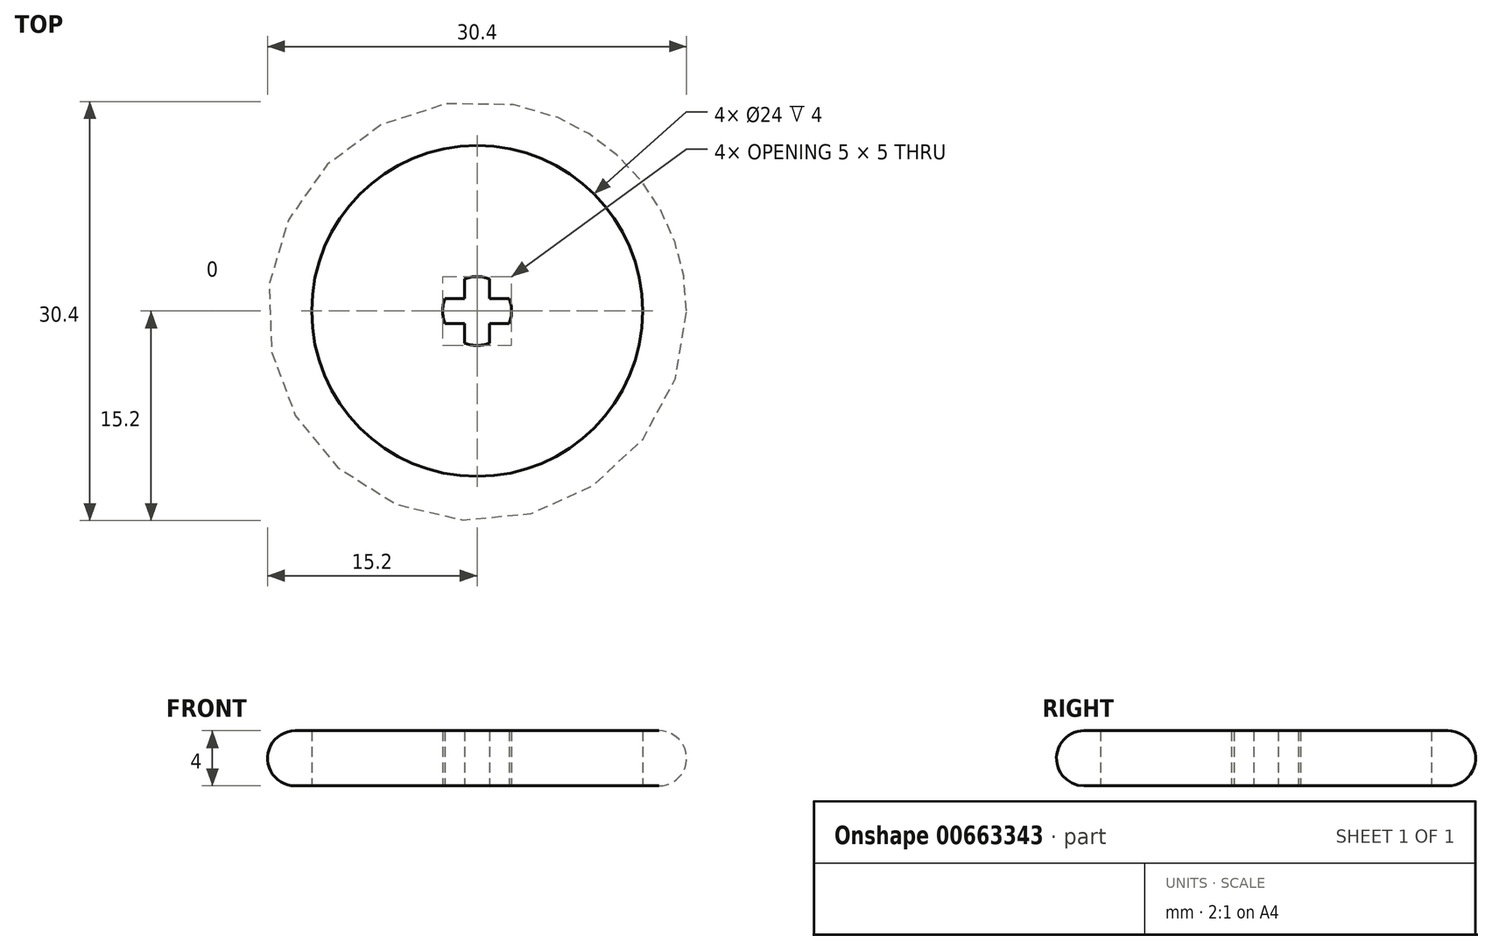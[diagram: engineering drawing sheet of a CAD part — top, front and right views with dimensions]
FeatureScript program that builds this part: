
annotation { "Feature Type Name" : "Feature", "Feature Type Description" : "" }
export const myFeature = defineFeature(function(context is Context, id is Id, definition is map)
    precondition{}
    {
        {
            var Q0;
            Q0=qCreatedBy(makeId("Top.planeOp"),FACE);
            var sketch = newSketch(context, id + "F0", { "sketchPlane" : qUnion([Q0])});
            skCircle(sketch, "E0", {"center": v(0, 0) * mm, "radius": 12 * mm});
            skArc(sketch, "E1", {"start": v(-0.9, -2.33) * mm, "mid": v(0, -2.5) * mm, "end": v(0.9, -2.33) * mm});
            skLineSegment(sketch, "E2.left", {"start": v(0.9, 2.33) * mm, "end": v(0.9, 0.9) * mm});
            skLineSegment(sketch, "E2.right", {"start": v(-0.9, 2.33) * mm, "end": v(-0.9, 0.9) * mm});
            skLineSegment(sketch, "E3.bottom", {"start": v(2.33, 0.9) * mm, "end": v(0.9, 0.9) * mm});
            skLineSegment(sketch, "E3.top", {"start": v(2.33, -0.9) * mm, "end": v(0.9, -0.9) * mm});
            skLineSegment(sketch, "E4.trimOffspring", {"start": v(-0.9, -0.9) * mm, "end": v(-0.9, -2.33) * mm});
            skLineSegment(sketch, "E5.trimOffspring", {"start": v(-0.9, 0.9) * mm, "end": v(-2.33, 0.9) * mm});
            skLineSegment(sketch, "E6.trimOffspring", {"start": v(0.9, -0.9) * mm, "end": v(0.9, -2.33) * mm});
            skLineSegment(sketch, "E7.trimOffspring", {"start": v(-0.9, -0.9) * mm, "end": v(-2.33, -0.9) * mm});
            skArc(sketch, "E8.trimOffspring", {"start": v(-2.33, 0.9) * mm, "mid": v(-2.5, 0) * mm, "end": v(-2.33, -0.9) * mm});
            skArc(sketch, "E9.trimOffspring", {"start": v(0.9, 2.33) * mm, "mid": v(0, 2.5) * mm, "end": v(-0.9, 2.33) * mm});
            skArc(sketch, "E10.trimOffspring", {"start": v(2.33, -0.9) * mm, "mid": v(2.5, 0) * mm, "end": v(2.33, 0.9) * mm});
            skCircle(sketch, "E11", {"center": v(0, 0) * mm, "radius": 15.2 * mm});
            skSolve(sketch);
        }
        {
            var Q0;
            Q0=makeQuery(id+"F0.imprint","IMPRINT",FACE,{"disambiguationData":[TD([[makeQuery(id+"F0.imprint","IMPRINT",EDGE,{"derivedFrom":sQuery(id+"F0.wireOp",EDGE,"E0")}),1.0]])]});
            extrude(context, id + "F1", {"entities" : qUnion([Q0]), "endBound" : BoundingType.SYMMETRIC, "depth" : 4 * mm, "offsetDistance" : 25 * mm});
        }
        {
            var Q0;
            Q0=makeQuery(id+"F0.imprint","IMPRINT",FACE,{"disambiguationData":[TD([[makeQuery(id+"F0.imprint","IMPRINT",EDGE,{"derivedFrom":sQuery(id+"F0.wireOp",EDGE,"E0")}),-1.0]])]});
            extrude(context, id + "F2", {"entities" : qUnion([Q0]), "endBound" : BoundingType.SYMMETRIC, "depth" : 4 * mm, "offsetDistance" : 25 * mm});
        }
        {
            var Q0;
            Q0=makeQuery(id+"F2.opExtrude","CAP_EDGE",EDGE,{"disambiguationData":[OSD([sQuery(id+"F0.wireOp",EDGE,"E11")])],"isStart":false});
            var Q1;
            Q1=makeQuery(id+"F2.opExtrude","CAP_EDGE",EDGE,{"disambiguationData":[OSD([sQuery(id+"F0.wireOp",EDGE,"E11")])],"isStart":true});
            fillet(context, id + "F3", {"entities" : qUnion([Q0, Q1]), "radius" : 2 * mm, "tangentPropagation" : true, "allowEdgeOverflow" : false});
        }
    });
